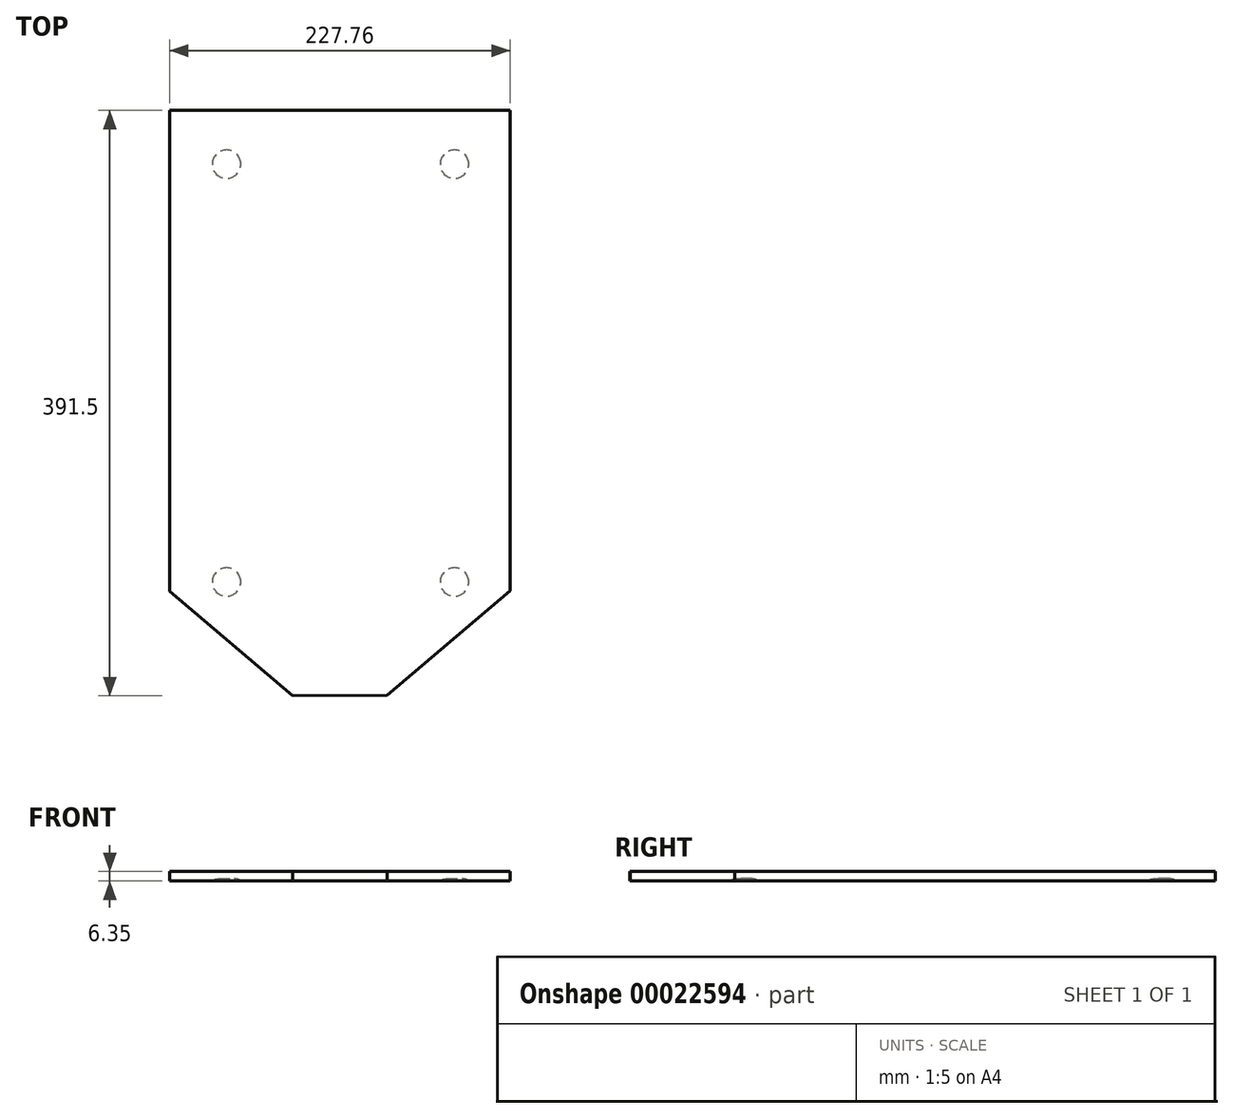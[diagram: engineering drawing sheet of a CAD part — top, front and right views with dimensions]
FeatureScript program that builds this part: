
annotation { "Feature Type Name" : "Feature", "Feature Type Description" : "" }
export const myFeature = defineFeature(function(context is Context, id is Id, definition is map)
    precondition{}
    {
        {
            var Q0;
            Q0=qCreatedBy(makeId("Top.planeOp"),FACE);
            var sketch = newSketch(context, id + "F0", { "sketchPlane" : qUnion([Q0])});
            skLineSegment(sketch, "E0.0", {"start": v(113.57, -116.69) * mm, "end": v(113.57, 204.65) * mm});
            skLineSegment(sketch, "E0.1", {"start": v(-114.2, 204.65) * mm, "end": v(-114.2, -117) * mm});
            skLineSegment(sketch, "E0.2", {"start": v(-114.2, -117) * mm, "end": v(-31.89, -186.85) * mm});
            skLineSegment(sketch, "E0.3", {"start": v(113.57, 204.65) * mm, "end": v(-114.2, 204.65) * mm});
            skLineSegment(sketch, "E0.4", {"start": v(-31.89, -186.85) * mm, "end": v(31.26, -186.54) * mm});
            skLineSegment(sketch, "E0.5", {"start": v(31.26, -186.54) * mm, "end": v(113.57, -116.69) * mm});
            skSolve(sketch);
        }
        {
            var Q0;
            Q0 = qSketchRegion(id + "F0", true);
            extrude(context, id + "F1", {"entities" : qUnion([Q0]), "depth" : 6.35 * mm});
        }
        {
            var Q0;
            Q0=makeQuery(id+"F1.opExtrude","CAP_FACE",FACE,{"disambiguationData":[OSD([sQuery(id+"F0.wireOp",EDGE,"E0.0"),sQuery(id+"F0.wireOp",EDGE,"E0.1"),sQuery(id+"F0.wireOp",EDGE,"E0.2"),sQuery(id+"F0.wireOp",EDGE,"E0.3"),sQuery(id+"F0.wireOp",EDGE,"E0.4"),sQuery(id+"F0.wireOp",EDGE,"E0.5")])],"isStart":true});
            var sketch = newSketch(context, id + "F2", { "sketchPlane" : qUnion([Q0])});
            skLineSegment(sketch, "E1.bottom", {"start": v(76.2, -168.75) * mm, "end": v(-76.2, -168.75) * mm});
            skLineSegment(sketch, "E1.top", {"start": v(76.2, 110.65) * mm, "end": v(-76.2, 110.65) * mm});
            skLineSegment(sketch, "E1.left", {"start": v(76.2, -168.75) * mm, "end": v(76.2, 110.65) * mm});
            skLineSegment(sketch, "E1.right", {"start": v(-76.2, -168.75) * mm, "end": v(-76.2, 110.65) * mm});
            skPoint(sketch, "E1.middle", {"position": v(0, -29.05) * mm});
            skCircle(sketch, "E2", {"center": v(-76.2, 110.65) * mm, "radius": 9.53 * mm});
            skCircle(sketch, "E3", {"center": v(76.2, 110.65) * mm, "radius": 9.53 * mm});
            skCircle(sketch, "E4", {"center": v(76.2, -168.75) * mm, "radius": 9.53 * mm});
            skCircle(sketch, "E5", {"center": v(-76.2, -168.75) * mm, "radius": 9.53 * mm});
            skSolve(sketch);
        }
        {
            var Q0;
            {var subQ0=sQuery(id+"F2.wireOp",EDGE,"E1.right");var subQ1=sQuery(id+"F2.wireOp",EDGE,"E1.top");var subQ2=makeQuery(id+"F2.imprint","INTERSECT",VERTEX,{"derivedFrom":[subQ1,subQ0]});Q0=makeQuery(id+"F2.imprint","IMPRINT",FACE,{"disambiguationData":[TD([[makeQuery(id+"F2.imprint","IMPRINT",EDGE,{"disambiguationData":[TD([[subQ2,1.0]])],"derivedFrom":subQ1}),-1.0]])]});}
            var Q1;
            {var subQ0=sQuery(id+"F2.wireOp",EDGE,"E1.right");var subQ1=sQuery(id+"F2.wireOp",EDGE,"E1.top");var subQ2=makeQuery(id+"F2.imprint","INTERSECT",VERTEX,{"derivedFrom":[subQ1,subQ0]});Q1=makeQuery(id+"F2.imprint","IMPRINT",FACE,{"disambiguationData":[TD([[makeQuery(id+"F2.imprint","IMPRINT",EDGE,{"disambiguationData":[TD([[subQ2,1.0]])],"derivedFrom":subQ1}),1.0]])]});}
            var Q2;
            {var subQ0=sQuery(id+"F2.wireOp",EDGE,"E1.left");var subQ1=sQuery(id+"F2.wireOp",EDGE,"E1.top");var subQ2=makeQuery(id+"F2.imprint","INTERSECT",VERTEX,{"derivedFrom":[subQ1,subQ0]});Q2=makeQuery(id+"F2.imprint","IMPRINT",FACE,{"disambiguationData":[TD([[makeQuery(id+"F2.imprint","IMPRINT",EDGE,{"disambiguationData":[TD([[subQ2,-1.0]])],"derivedFrom":subQ1}),-1.0]])]});}
            var Q3;
            {var subQ0=sQuery(id+"F2.wireOp",EDGE,"E1.left");var subQ1=sQuery(id+"F2.wireOp",EDGE,"E1.top");var subQ2=makeQuery(id+"F2.imprint","INTERSECT",VERTEX,{"derivedFrom":[subQ1,subQ0]});Q3=makeQuery(id+"F2.imprint","IMPRINT",FACE,{"disambiguationData":[TD([[makeQuery(id+"F2.imprint","IMPRINT",EDGE,{"disambiguationData":[TD([[subQ2,-1.0]])],"derivedFrom":subQ1}),1.0]])]});}
            var Q4;
            {var subQ0=sQuery(id+"F2.wireOp",EDGE,"E1.left");var subQ1=sQuery(id+"F2.wireOp",EDGE,"E1.bottom");var subQ2=makeQuery(id+"F2.imprint","INTERSECT",VERTEX,{"derivedFrom":[subQ1,subQ0]});Q4=makeQuery(id+"F2.imprint","IMPRINT",FACE,{"disambiguationData":[TD([[makeQuery(id+"F2.imprint","IMPRINT",EDGE,{"disambiguationData":[TD([[subQ2,-1.0]])],"derivedFrom":subQ1}),-1.0]])]});}
            var Q5;
            {var subQ0=sQuery(id+"F2.wireOp",EDGE,"E1.left");var subQ1=sQuery(id+"F2.wireOp",EDGE,"E1.bottom");var subQ2=makeQuery(id+"F2.imprint","INTERSECT",VERTEX,{"derivedFrom":[subQ1,subQ0]});Q5=makeQuery(id+"F2.imprint","IMPRINT",FACE,{"disambiguationData":[TD([[makeQuery(id+"F2.imprint","IMPRINT",EDGE,{"disambiguationData":[TD([[subQ2,-1.0]])],"derivedFrom":subQ1}),1.0]])]});}
            var Q6;
            {var subQ0=sQuery(id+"F2.wireOp",EDGE,"E1.right");var subQ1=sQuery(id+"F2.wireOp",EDGE,"E1.bottom");var subQ2=makeQuery(id+"F2.imprint","INTERSECT",VERTEX,{"derivedFrom":[subQ1,subQ0]});Q6=makeQuery(id+"F2.imprint","IMPRINT",FACE,{"disambiguationData":[TD([[makeQuery(id+"F2.imprint","IMPRINT",EDGE,{"disambiguationData":[TD([[subQ2,1.0]])],"derivedFrom":subQ1}),-1.0]])]});}
            var Q7;
            {var subQ0=sQuery(id+"F2.wireOp",EDGE,"E1.right");var subQ1=sQuery(id+"F2.wireOp",EDGE,"E1.bottom");var subQ2=makeQuery(id+"F2.imprint","INTERSECT",VERTEX,{"derivedFrom":[subQ1,subQ0]});Q7=makeQuery(id+"F2.imprint","IMPRINT",FACE,{"disambiguationData":[TD([[makeQuery(id+"F2.imprint","IMPRINT",EDGE,{"disambiguationData":[TD([[subQ2,1.0]])],"derivedFrom":subQ1}),1.0]])]});}
            var Q8;
            Q8=sQuery(id+"F2.wireOp",EDGE,"E2");
            var Q9;
            Q9=sQuery(id+"F2.wireOp",EDGE,"E3");
            var Q10;
            Q10=sQuery(id+"F2.wireOp",EDGE,"E4");
            var Q11;
            Q11=sQuery(id+"F2.wireOp",EDGE,"E5");
            extrude(context, id + "F3", {"entities" : qUnion([Q0, Q1, Q2, Q3, Q4, Q5, Q6, Q7]), "operationType" : NewBodyOperationType.REMOVE, "surfaceEntities" : qUnion([Q8, Q9, Q10, Q11]), "oppositeDirection" : true, "depth" : 1.59 * mm});
        }
        {
            var Q0;
            Q0=makeQuery(id+"F3.boolean.opBoolean","COPY",FACE,{"derivedFrom":makeQuery(id+"F3.opExtrude","CAP_FACE",FACE,{"disambiguationData":[OSD([sQuery(id+"F2.wireOp",EDGE,"E2")])],"isStart":false})});
            var Q1;
            Q1=makeQuery(id+"F3.boolean.opBoolean","COPY",FACE,{"derivedFrom":makeQuery(id+"F3.opExtrude","CAP_FACE",FACE,{"disambiguationData":[OSD([sQuery(id+"F2.wireOp",EDGE,"E3")])],"isStart":false})});
            var Q2;
            Q2=makeQuery(id+"F3.boolean.opBoolean","COPY",FACE,{"derivedFrom":makeQuery(id+"F3.opExtrude","CAP_FACE",FACE,{"disambiguationData":[OSD([sQuery(id+"F2.wireOp",EDGE,"E5")])],"isStart":false})});
            var Q3;
            Q3=makeQuery(id+"F3.boolean.opBoolean","COPY",FACE,{"derivedFrom":makeQuery(id+"F3.opExtrude","CAP_FACE",FACE,{"disambiguationData":[OSD([sQuery(id+"F2.wireOp",EDGE,"E4")])],"isStart":false})});
            fillet(context, id + "F4", {"entities" : qUnion([Q0, Q1, Q2, Q3]), "radius" : 6.35 * mm, "tangentPropagation" : true, "allowEdgeOverflow" : false});
        }
    });
